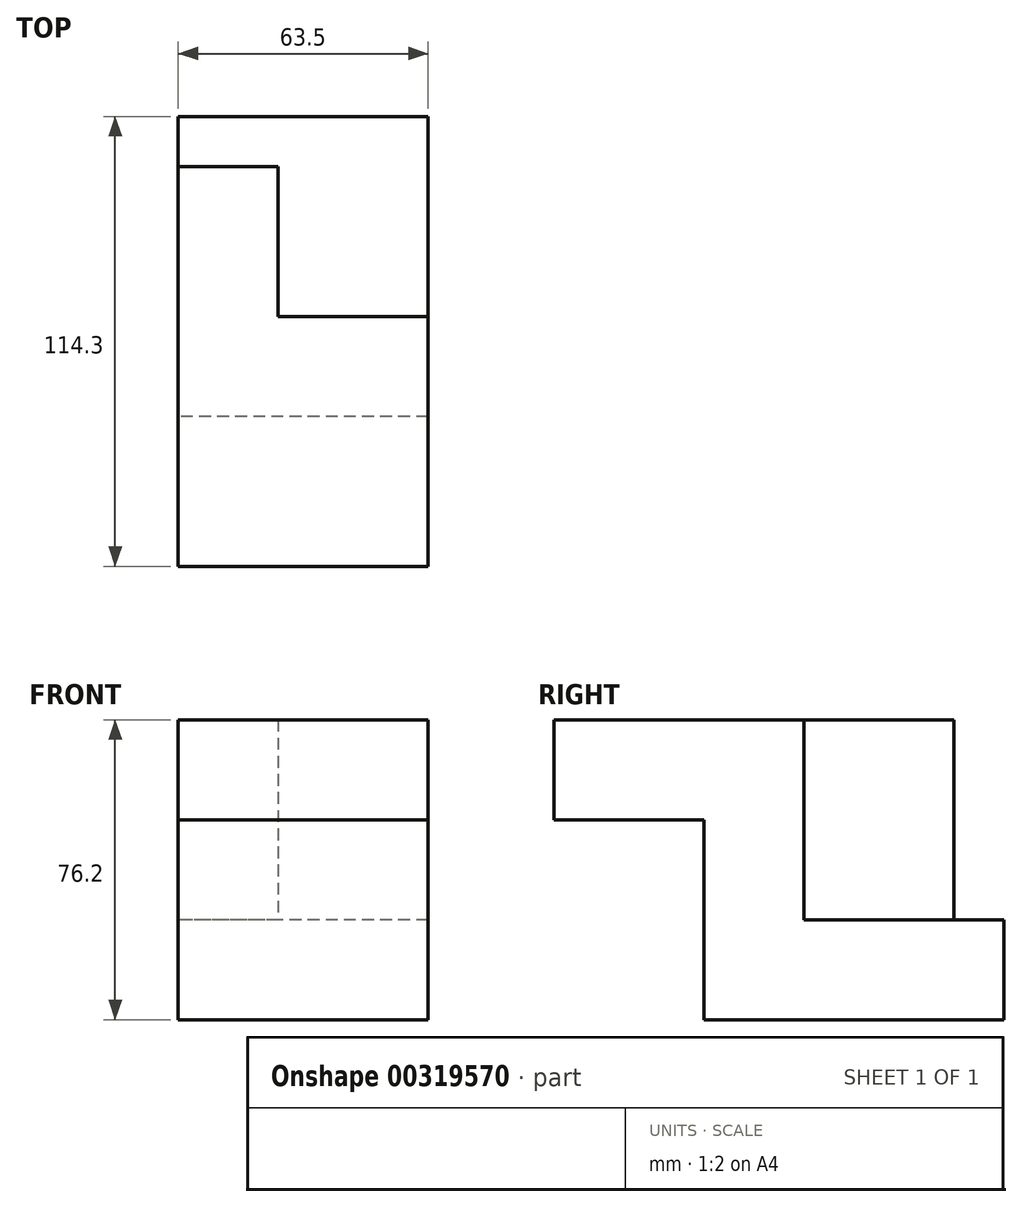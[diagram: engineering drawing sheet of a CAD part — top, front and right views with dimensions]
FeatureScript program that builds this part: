
annotation { "Feature Type Name" : "Feature", "Feature Type Description" : "" }
export const myFeature = defineFeature(function(context is Context, id is Id, definition is map)
    precondition{}
    {
        {
            var Q0;
            Q0=qCreatedBy(makeId("Right.planeOp"),FACE);
            var sketch = newSketch(context, id + "F0", { "sketchPlane" : qUnion([Q0])});
            skLineSegment(sketch, "E0", {"start": v(-55.94, 31.32) * mm, "end": v(7.56, 31.32) * mm});
            skLineSegment(sketch, "E1", {"start": v(7.56, 31.32) * mm, "end": v(7.56, -19.48) * mm});
            skLineSegment(sketch, "E2", {"start": v(7.56, -19.48) * mm, "end": v(58.36, -19.48) * mm});
            skLineSegment(sketch, "E3", {"start": v(58.36, -19.48) * mm, "end": v(58.36, -44.88) * mm});
            skLineSegment(sketch, "E4", {"start": v(58.36, -44.88) * mm, "end": v(-17.84, -44.88) * mm});
            skLineSegment(sketch, "E5", {"start": v(-17.84, -44.88) * mm, "end": v(-17.84, 5.92) * mm});
            skLineSegment(sketch, "E6", {"start": v(-17.84, 5.92) * mm, "end": v(-55.94, 5.92) * mm});
            skLineSegment(sketch, "E7", {"start": v(-55.94, 5.92) * mm, "end": v(-55.94, 31.32) * mm});
            skSolve(sketch);
        }
        {
            var Q0;
            Q0=makeQuery(id+"F0.imprint","IMPRINT",FACE,{"disambiguationData":[TD([[makeQuery(id+"F0.imprint","IMPRINT",EDGE,{"derivedFrom":sQuery(id+"F0.wireOp",EDGE,"E0")}),-1.0]])]});
            extrude(context, id + "F1", {"entities" : qUnion([Q0]), "depth" : 63.5 * mm});
        }
        {
            var Q0;
            Q0=makeQuery(id+"F1.opExtrude","SWEPT_FACE",FACE,{"disambiguationData":[OSD([sQuery(id+"F0.wireOp",EDGE,"E1")])]});
            var sketch = newSketch(context, id + "F2", { "sketchPlane" : qUnion([Q0])});
            skLineSegment(sketch, "E8", {"start": v(0, 31.32) * mm, "end": v(-25.4, 31.32) * mm});
            skLineSegment(sketch, "E9", {"start": v(-25.4, 31.32) * mm, "end": v(-25.4, -19.48) * mm});
            skLineSegment(sketch, "E10", {"start": v(-25.4, -19.48) * mm, "end": v(0, -19.48) * mm});
            skLineSegment(sketch, "E11", {"start": v(0, -19.48) * mm, "end": v(0, 31.32) * mm});
            skSolve(sketch);
        }
        {
            var Q0;
            Q0=makeQuery(id+"F2.imprint","IMPRINT",FACE,{"disambiguationData":[TD([[makeQuery(id+"F2.imprint","IMPRINT",EDGE,{"derivedFrom":sQuery(id+"F2.wireOp",EDGE,"E8")}),-1.0]])]});
            extrude(context, id + "F3", {"entities" : qUnion([Q0]), "operationType" : NewBodyOperationType.ADD, "depth" : 38.1 * mm});
        }
    });
